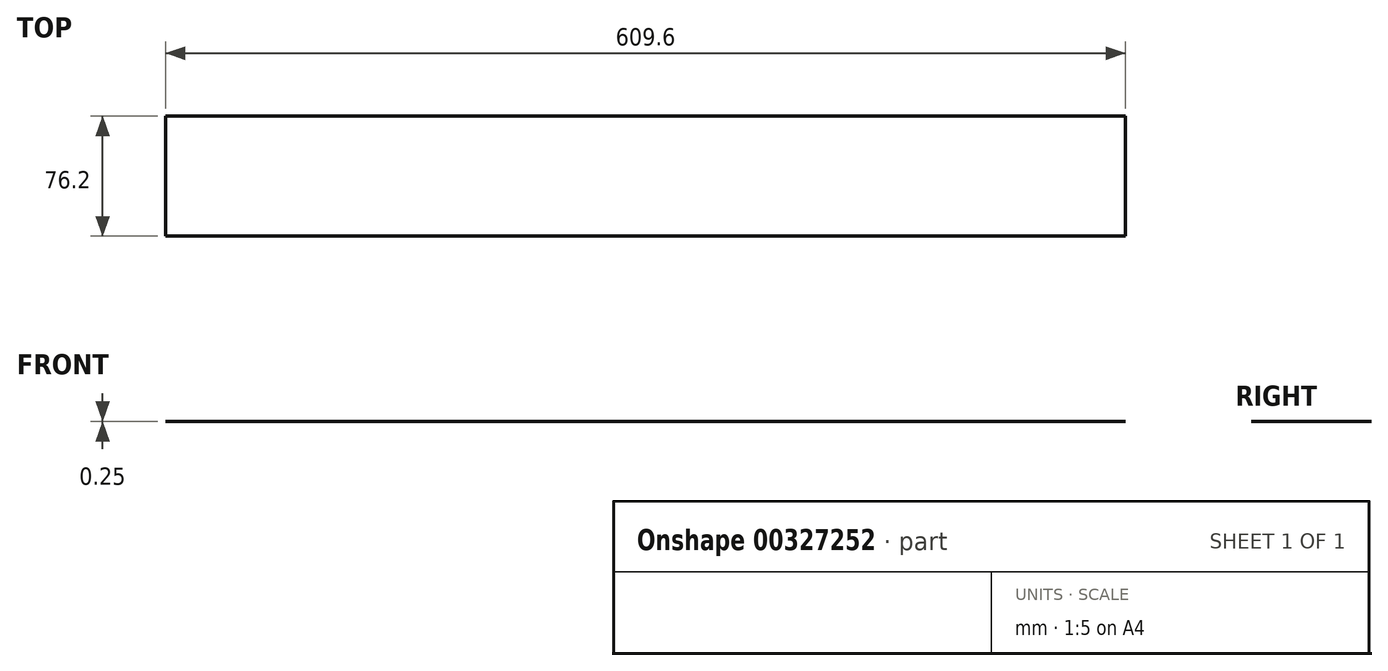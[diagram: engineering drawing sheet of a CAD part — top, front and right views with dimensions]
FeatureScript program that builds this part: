
annotation { "Feature Type Name" : "Feature", "Feature Type Description" : "" }
export const myFeature = defineFeature(function(context is Context, id is Id, definition is map)
    precondition{}
    {
        {
            assignVariable(context, id + "F0", {"name" : "THKNS", "anyValue" : .25});
        }
        {
            var Q0;
            Q0=qCreatedBy(makeId("Top.planeOp"),FACE);
            var sketch = newSketch(context, id + "F1", { "sketchPlane" : qUnion([Q0])});
            skLineSegment(sketch, "E0.bottom", {"start": v(0, 76.2) * mm, "end": v(609.6, 76.2) * mm});
            skLineSegment(sketch, "E0.top", {"start": v(0, 0) * mm, "end": v(609.6, 0) * mm});
            skLineSegment(sketch, "E0.left", {"start": v(0, 76.2) * mm, "end": v(0, 0) * mm});
            skLineSegment(sketch, "E0.right", {"start": v(609.6, 76.2) * mm, "end": v(609.6, 0) * mm});
            skSolve(sketch);
        }
        {
            var Q0;
            Q0=qSketchRegion(id+"F1",true);
            extrude(context, id + "F2", {"entities" : qUnion([Q0]), "depth" : (getVariable(context, 'THKNS')) * mm});
        }
    });
